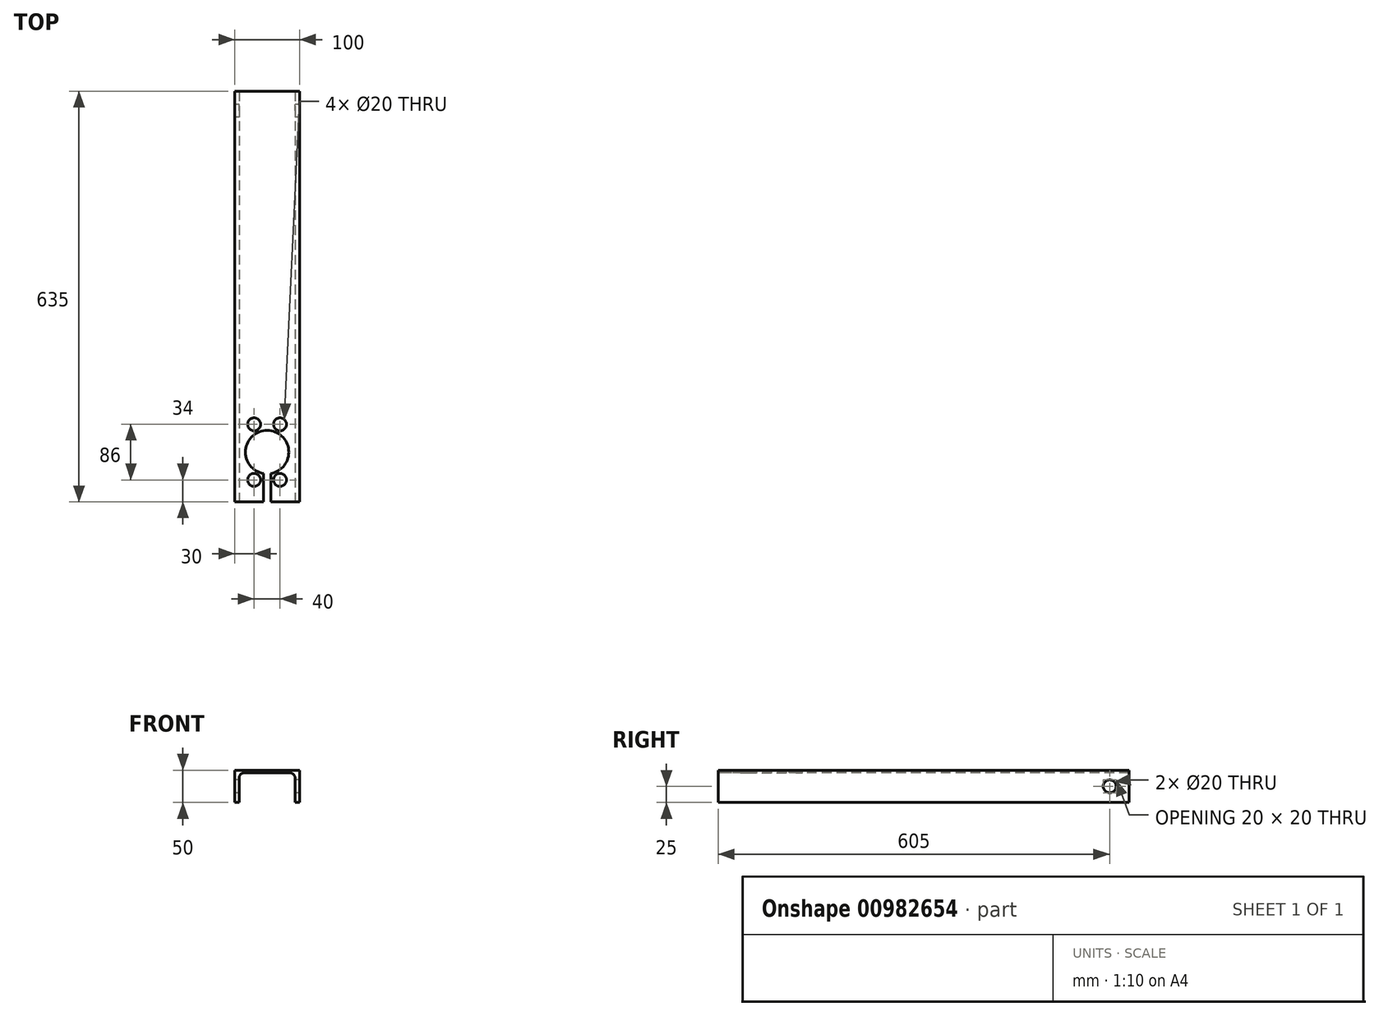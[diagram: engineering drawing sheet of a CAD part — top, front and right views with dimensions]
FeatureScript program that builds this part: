
annotation { "Feature Type Name" : "Feature", "Feature Type Description" : "" }
export const myFeature = defineFeature(function(context is Context, id is Id, definition is map)
    precondition{}
    {
        {
            var Q0;
            Q0=qCreatedBy(makeId("Front.planeOp"),FACE);
            var sketch = newSketch(context, id + "F0", { "sketchPlane" : qUnion([Q0])});
            skLineSegment(sketch, "E0", {"start": v(0, 16.82) * mm, "end": v(0, -29.37) * mm, "construction": true});
            skLineSegment(sketch, "E1", {"start": v(0, 0) * mm, "end": v(-50, 0) * mm});
            skLineSegment(sketch, "E2", {"start": v(-50, 0) * mm, "end": v(-50, -50) * mm});
            skLineSegment(sketch, "E3", {"start": v(-50, -50) * mm, "end": v(-43.3, -50) * mm});
            skLineSegment(sketch, "E4", {"start": v(-43.3, -50) * mm, "end": v(-43.3, -12.2) * mm});
            skLineSegment(sketch, "E5", {"start": v(-35.3, -4.2) * mm, "end": v(0, -4.2) * mm});
            skPoint(sketch, "E6.visualSharp", {"position": v(-43.3, -4.2) * mm});
            skArc(sketch, "E6.filletArc", {"start": v(-35.3, -4.2) * mm, "mid": v(-40.96, -6.54) * mm, "end": v(-43.3, -12.2) * mm});
            skLineSegment(sketch, "E7.MirrorCS", {"start": v(50, -50) * mm, "end": v(43.3, -50) * mm});
            skArc(sketch, "E8.MirrorCS", {"start": v(35.3, -4.2) * mm, "mid": v(40.96, -6.54) * mm, "end": v(43.3, -12.2) * mm});
            skLineSegment(sketch, "E9.MirrorCS", {"start": v(50, 0) * mm, "end": v(50, -50) * mm});
            skLineSegment(sketch, "E10.MirrorCS", {"start": v(43.3, -50) * mm, "end": v(43.3, -12.2) * mm});
            skLineSegment(sketch, "E11.MirrorCS", {"start": v(0, 0) * mm, "end": v(50, 0) * mm});
            skLineSegment(sketch, "E12.MirrorCS", {"start": v(35.3, -4.2) * mm, "end": v(0, -4.2) * mm});
            skPoint(sketch, "E13.MirrorP", {"position": v(43.3, -4.2) * mm});
            skSolve(sketch);
        }
        {
            var Q0;
            Q0 = qSketchRegion(id + "F0", true);
            extrude(context, id + "F1", {"entities" : qUnion([Q0]), "oppositeDirection" : true, "depth" : 635 * mm, "offsetDistance" : 25 * mm});
        }
        {
            var Q0;
            Q0=makeQuery(id+"F1.opExtrude","SWEPT_FACE",FACE,{"disambiguationData":[OSD([sQuery(id+"F0.wireOp",EDGE,"E1"),sQuery(id+"F0.wireOp",EDGE,"E11.MirrorCS")])]});
            var sketch = newSketch(context, id + "F2", { "sketchPlane" : qUnion([Q0])});
            skArc(sketch, "E14", {"start": v(5.75, 44) * mm, "mid": v(0, 110.5) * mm, "end": v(-5.75, 44) * mm});
            skLineSegment(sketch, "E15", {"start": v(-5.75, 44) * mm, "end": v(-5.75, 0) * mm});
            skLineSegment(sketch, "E16.MirrorCS", {"start": v(5.75, 44) * mm, "end": v(5.75, 0) * mm});
            skLineSegment(sketch, "E17", {"start": v(-5.75, 0) * mm, "end": v(5.75, 0) * mm});
            skSolve(sketch);
        }
        {
            var Q0;
            Q0 = qSketchRegion(id + "F2", true);
            extrude(context, id + "F3", {"entities" : qUnion([Q0]), "operationType" : NewBodyOperationType.REMOVE, "endBound" : BoundingType.UP_TO_NEXT, "oppositeDirection" : true, "depth" : 25 * mm, "offsetDistance" : 25 * mm});
        }
        {
            var Q0;
            Q0=makeQuery(id+"F1.opExtrude","SWEPT_FACE",FACE,{"disambiguationData":[OSD([sQuery(id+"F0.wireOp",EDGE,"E1"),sQuery(id+"F0.wireOp",EDGE,"E11.MirrorCS")])]});
            var sketch = newSketch(context, id + "F4", { "sketchPlane" : qUnion([Q0])});
            skCircle(sketch, "E18", {"center": v(-20, 34) * mm, "radius": 10 * mm});
            skLineSegment(sketch, "E19", {"start": v(0, 77) * mm, "end": v(-93.7, 77) * mm, "construction": true});
            skCircle(sketch, "E20.0.1.0", {"center": v(-20, 120) * mm, "radius": 10 * mm});
            skCircle(sketch, "E20.1.0.0", {"center": v(20, 34) * mm, "radius": 10 * mm});
            skCircle(sketch, "E20.1.1.0", {"center": v(20, 120) * mm, "radius": 10 * mm});
            skLineSegment(sketch, "E20.direction1", {"start": v(-20, 34) * mm, "end": v(20, 34) * mm, "construction": true});
            skLineSegment(sketch, "E20.direction2", {"start": v(-20, 34) * mm, "end": v(-20, 120) * mm, "construction": true});
            skSolve(sketch);
        }
        {
            var Q0;
            Q0 = qSketchRegion(id + "F4", true);
            extrude(context, id + "F5", {"entities" : qUnion([Q0]), "operationType" : NewBodyOperationType.REMOVE, "endBound" : BoundingType.UP_TO_NEXT, "oppositeDirection" : true, "depth" : 25 * mm, "offsetDistance" : 25 * mm});
        }
        {
            var Q0;
            Q0=makeQuery(id+"F1.opExtrude","SWEPT_FACE",FACE,{"disambiguationData":[OSD([sQuery(id+"F0.wireOp",EDGE,"E2")])]});
            var sketch = newSketch(context, id + "F6", { "sketchPlane" : qUnion([Q0])});
            skCircle(sketch, "E21", {"center": v(-605, -25) * mm, "radius": 10 * mm});
            skSolve(sketch);
        }
        {
            var Q0;
            Q0 = qSketchRegion(id + "F6", true);
            var Q1;
            Q1=makeQuery(id+"F1.opExtrude","SWEPT_FACE",FACE,{"disambiguationData":[OSD([sQuery(id+"F0.wireOp",EDGE,"E9.MirrorCS")])]});
            extrude(context, id + "F7", {"entities" : qUnion([Q0]), "operationType" : NewBodyOperationType.REMOVE, "endBound" : BoundingType.UP_TO_SURFACE, "oppositeDirection" : true, "depth" : 25 * mm, "endBoundEntityFace" : qUnion([Q1]), "offsetDistance" : 25 * mm});
        }
    });
